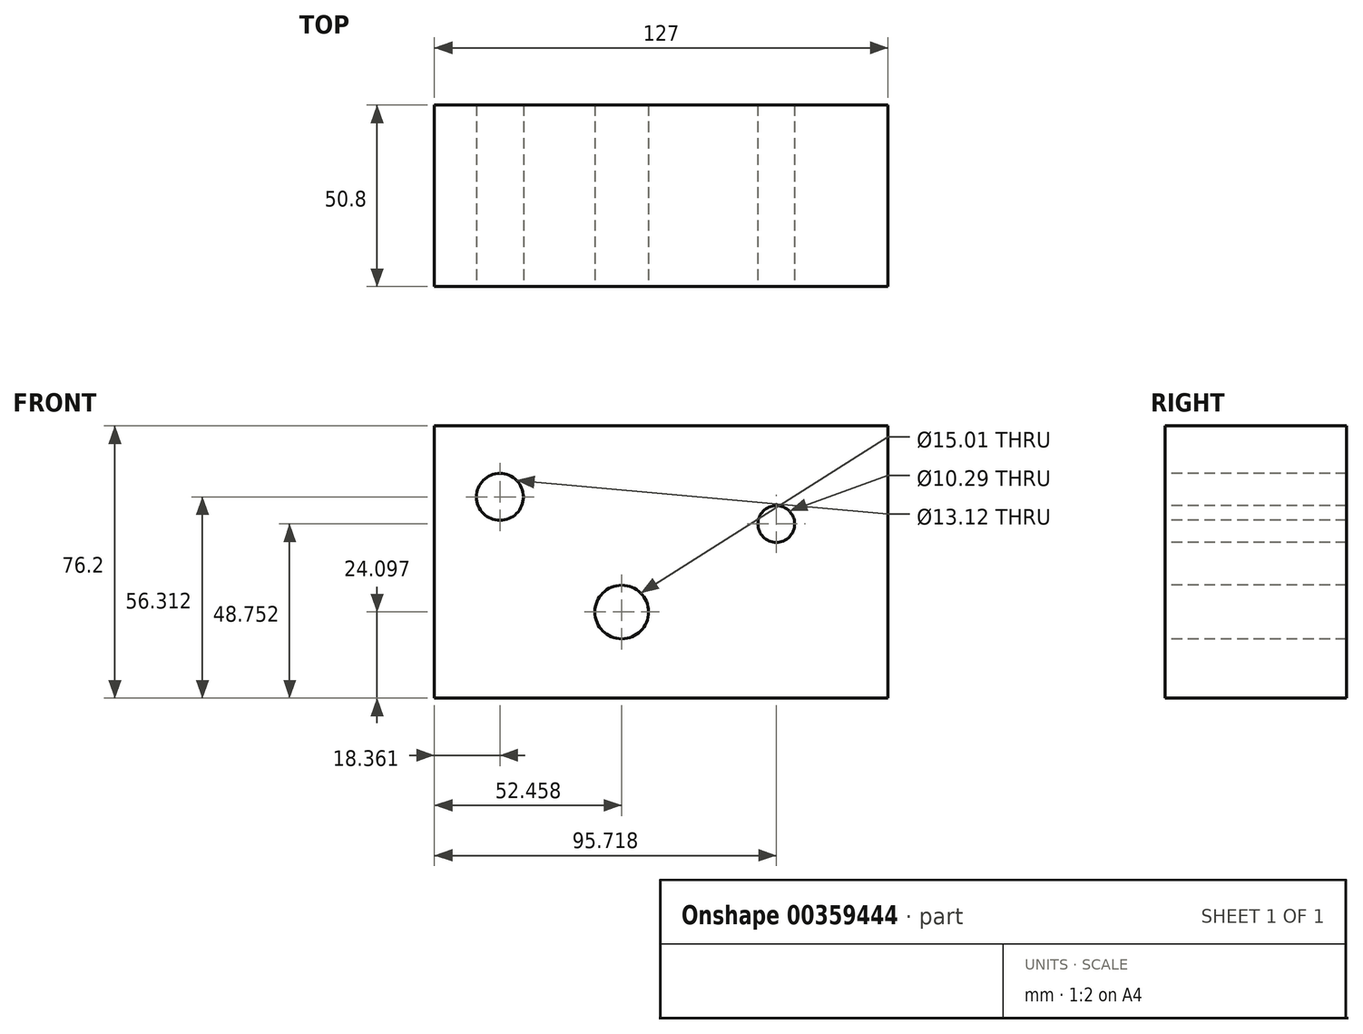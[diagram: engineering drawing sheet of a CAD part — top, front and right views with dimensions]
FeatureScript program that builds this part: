
annotation { "Feature Type Name" : "Feature", "Feature Type Description" : "" }
export const myFeature = defineFeature(function(context is Context, id is Id, definition is map)
    precondition{}
    {
        {
            var Q0;
            Q0=qCreatedBy(makeId("Front.planeOp"),FACE);
            var sketch = newSketch(context, id + "F0", { "sketchPlane" : qUnion([Q0])});
            skLineSegment(sketch, "E0.bottom", {"start": v(63.5, -38.1) * mm, "end": v(-63.5, -38.1) * mm});
            skLineSegment(sketch, "E0.top", {"start": v(63.5, 38.1) * mm, "end": v(-63.5, 38.1) * mm});
            skLineSegment(sketch, "E0.left", {"start": v(63.5, -38.1) * mm, "end": v(63.5, 38.1) * mm});
            skLineSegment(sketch, "E0.right", {"start": v(-63.5, -38.1) * mm, "end": v(-63.5, 38.1) * mm});
            skPoint(sketch, "E0.middle", {"position": v(0, 0) * mm});
            skSolve(sketch);
        }
        {
            var Q0;
            Q0=makeQuery(id+"F0.imprint","IMPRINT",FACE,{"disambiguationData":[TD([[makeQuery(id+"F0.imprint","IMPRINT",EDGE,{"derivedFrom":sQuery(id+"F0.wireOp",EDGE,"E0.bottom")}),-1.0]])]});
            extrude(context, id + "F1", {"entities" : qUnion([Q0]), "endBound" : BoundingType.SYMMETRIC, "oppositeDirection" : true, "depth" : 50.8 * mm});
        }
        {
            var Q0;
            Q0=makeQuery(id+"F1.opExtrude","CAP_FACE",FACE,{"disambiguationData":[OSD([sQuery(id+"F0.wireOp",EDGE,"E0.bottom"),sQuery(id+"F0.wireOp",EDGE,"E0.top"),sQuery(id+"F0.wireOp",EDGE,"E0.left"),sQuery(id+"F0.wireOp",EDGE,"E0.right")])],"isStart":true});
            var sketch = newSketch(context, id + "F2", { "sketchPlane" : qUnion([Q0])});
            skCircle(sketch, "E1", {"center": v(-45.14, 18.21) * mm, "radius": 6.56 * mm});
            skCircle(sketch, "E2", {"center": v(32.22, 10.65) * mm, "radius": 5.14 * mm});
            skCircle(sketch, "E3", {"center": v(-11.04, -14) * mm, "radius": 7.5 * mm});
            skSolve(sketch);
        }
        {
            var Q0;
            Q0 = qSketchRegion(id + "F2", true);
            extrude(context, id + "F3", {"entities" : qUnion([Q0]), "operationType" : NewBodyOperationType.REMOVE, "endBound" : BoundingType.THROUGH_ALL, "oppositeDirection" : true, "depth" : 25.4 * mm});
        }
    });
